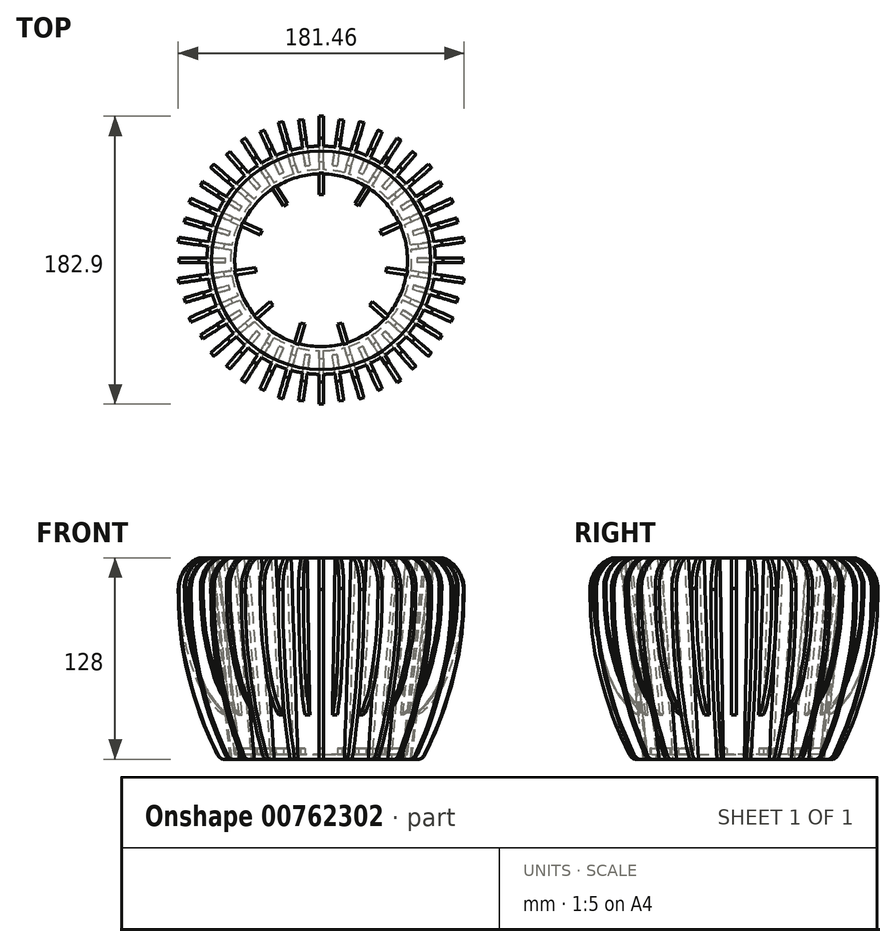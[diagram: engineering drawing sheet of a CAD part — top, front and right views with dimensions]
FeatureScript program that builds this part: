
annotation { "Feature Type Name" : "Feature", "Feature Type Description" : "" }
export const myFeature = defineFeature(function(context is Context, id is Id, definition is map)
    precondition{}
    {
        {
            var Q0;
            Q0=qCreatedBy(makeId("Top.planeOp"),FACE);
            var sketch = newSketch(context, id + "F0", { "sketchPlane" : qUnion([Q0])});
            skCircle(sketch, "E0", {"center": v(0, 0) * mm, "radius": 57.5 * mm});
            skSolve(sketch);
        }
        {
            var Q0;
            Q0=qCreatedBy(makeId("Top.planeOp"),FACE);
            cPlane(context, id + "F1", {"entities" : qUnion([Q0]), "cplaneType" : CPlaneType.OFFSET, "offset" : 128 * mm, "width" : 150 * mm, "height" : 150 * mm});
        }
        {
            var Q0;
            Q0=qCreatedBy(id+"F1.planeOp",FACE);
            var sketch = newSketch(context, id + "F2", { "sketchPlane" : qUnion([Q0])});
            skCircle(sketch, "E1", {"center": v(0, 0) * mm, "radius": 72.5 * mm});
            skSolve(sketch);
        }
        {
            var Q0;
            Q0=makeQuery(id+"F0.imprint","IMPRINT",FACE,{"disambiguationData":[TD([[makeQuery(id+"F0.imprint","IMPRINT",EDGE,{"derivedFrom":sQuery(id+"F0.wireOp",EDGE,"E0")}),1.0]])]});
            var Q1;
            Q1=makeQuery(id+"F2.imprint","IMPRINT",FACE,{"disambiguationData":[TD([[makeQuery(id+"F2.imprint","IMPRINT",EDGE,{"derivedFrom":sQuery(id+"F2.wireOp",EDGE,"E1")}),1.0]])]});
            loft(context, id + "F3", {"sheetProfilesArray" : [{ "sheetProfileEntities" : qUnion([Q0]) }, { "sheetProfileEntities" : qUnion([Q1]) }]});
        }
        {
            var Q0;
            Q0=makeQuery(id+"F3.opLoft","CAP_FACE",FACE,{"disambiguationData":[OSD([makeQuery(id+"F2.imprint","IMPRINT",FACE,{"disambiguationData":[TD([[makeQuery(id+"F2.imprint","IMPRINT",EDGE,{"derivedFrom":sQuery(id+"F2.wireOp",EDGE,"E1")}),1.0]])]})])],"isStart":true});
            var sketch = newSketch(context, id + "F4", { "sketchPlane" : qUnion([Q0])});
            skCircle(sketch, "E2", {"center": v(0, 0) * mm, "radius": 69.5 * mm});
            skSolve(sketch);
        }
        {
            var Q0;
            Q0=makeQuery(id+"F3.opLoft","CAP_FACE",FACE,{"disambiguationData":[OSD([makeQuery(id+"F0.imprint","IMPRINT",FACE,{"disambiguationData":[TD([[makeQuery(id+"F0.imprint","IMPRINT",EDGE,{"derivedFrom":sQuery(id+"F0.wireOp",EDGE,"E0")}),1.0]])]})])],"isStart":true});
            var sketch = newSketch(context, id + "F5", { "sketchPlane" : qUnion([Q0])});
            skCircle(sketch, "E3", {"center": v(0, 0) * mm, "radius": 54.5 * mm});
            skSolve(sketch);
        }
        {
            var Q1;
            Q1=makeQuery(id+"F5.imprint","IMPRINT",FACE,{"disambiguationData":[TD([[makeQuery(id+"F5.imprint","IMPRINT",EDGE,{"derivedFrom":sQuery(id+"F5.wireOp",EDGE,"E3")}),1.0]])]});
            var Q2;
            Q2=makeQuery(id+"F4.imprint","IMPRINT",FACE,{"disambiguationData":[TD([[makeQuery(id+"F4.imprint","IMPRINT",EDGE,{"derivedFrom":sQuery(id+"F4.wireOp",EDGE,"E2")}),1.0]])]});
            loft(context, id + "F6", {"operationType" : NewBodyOperationType.REMOVE, "sheetProfilesArray" : [{ "sheetProfileEntities" : qUnion([Q1]) }, { "sheetProfileEntities" : qUnion([Q2]) }]});
        }
        {
            var Q0;
            Q0=makeQuery(id+"F5.imprint","IMPRINT",FACE,{"disambiguationData":[TD([[makeQuery(id+"F5.imprint","IMPRINT",EDGE,{"derivedFrom":sQuery(id+"F5.wireOp",EDGE,"E3")}),1.0]])]});
            var Q1;
            Q1=makeQuery(id+"F5.imprint","IMPRINT",FACE,{"disambiguationData":[TD([[makeQuery(id+"F5.imprint","IMPRINT",EDGE,{"derivedFrom":sQuery(id+"F5.wireOp",EDGE,"E3")}),-1.0]])]});
            extrude(context, id + "F7", {"entities" : qUnion([Q0, Q1]), "operationType" : NewBodyOperationType.ADD, "oppositeDirection" : true, "depth" : 3 * mm, "offsetDistance" : 25 * mm});
        }
        {
            var Q0;
            Q0=qCreatedBy(makeId("Front.planeOp"),FACE);
            var sketch = newSketch(context, id + "F8", { "sketchPlane" : qUnion([Q0])});
            skLineSegment(sketch, "E4", {"start": v(-1.5, 0) * mm, "end": v(1.5, 0) * mm});
            skLineSegment(sketch, "E5", {"start": v(1.5, 0) * mm, "end": v(1.5, 128) * mm});
            skLineSegment(sketch, "E6", {"start": v(1.5, 128) * mm, "end": v(-1.5, 128) * mm});
            skLineSegment(sketch, "E7", {"start": v(-1.5, 128) * mm, "end": v(-1.5, 0) * mm});
            skSolve(sketch);
        }
        {
            var Q0;
            Q0 = qSketchRegion(id + "F8", true);
            var Q1;
            Q1=makeQuery(id+"F3.opLoft","SWEPT_FACE",FACE,{"disambiguationData":[OSD([sQuery(id+"F0.wireOp",EDGE,"E0"),sQuery(id+"F2.wireOp",EDGE,"E1")])]});
            extrude(context, id + "F9", {"entities" : qUnion([Q0]), "operationType" : NewBodyOperationType.ADD, "oppositeDirection" : true, "depth" : 92.8 * mm, "offsetDistance" : 25 * mm, "hasSecondDirection" : true, "secondDirectionBound" : SecondDirectionBoundingType.UP_TO_SURFACE, "secondDirectionOppositeDirection" : true, "secondDirectionDepth" : 87.6 * mm, "secondDirectionBoundEntityFace" : qUnion([Q1])});
        }
        {
            var Q0;
            Q0=makeQuery(id+"F9.opExtrude","SWEPT_FACE",FACE,{"disambiguationData":[OSD([sQuery(id+"F8.wireOp",EDGE,"E7")])]});
            var sketch = newSketch(context, id + "F10", { "sketchPlane" : qUnion([Q0])});
            skPoint(sketch, "E8", {"position": v(-70.14, 108) * mm});
            skPoint(sketch, "E9", {"position": v(-77.48, 128) * mm});
            skArc(sketch, "E10", {"start": v(-77.48, 128) * mm, "mid": v(-87.61, 120.2) * mm, "end": v(-91.45, 108) * mm});
            skPoint(sketch, "E11", {"position": v(-62.48, 0) * mm});
            skLineSegment(sketch, "E12", {"start": v(-57.48, 0) * mm, "end": v(-62.48, 0) * mm});
            skFitSpline(sketch, "E13", {"points": [v(-62.48, 0) * mm, v(-64.01, 0.32) * mm, v(-65.44, 1.34) * mm, v(-67.06, 4.33) * mm, v(-75.69, 23.58) * mm, v(-88.98, 71.9) * mm, v(-91.45, 108) * mm], "startDerivative": vector(-27.52, 3.42) * mm, "endDerivative": vector(-1.61, 124.86) * mm});
            skLineSegment(sketch, "E14", {"start": v(-72.48, 128) * mm, "end": v(-77.48, 128) * mm});
            skSolve(sketch);
        }
        {
            var Q0;
            {var subQ5=sQuery(id+"F10.wireOp",EDGE,"E10");Q0=makeQuery(id+"F10.imprint","IMPRINT",FACE,{"disambiguationData":[TD([[makeQuery(id+"F10.imprint","IMPRINT",EDGE,{"derivedFrom":subQ5}),-1.0]])]});}
            extrude(context, id + "F11", {"entities" : qUnion([Q0]), "operationType" : NewBodyOperationType.REMOVE, "oppositeDirection" : true, "depth" : 3 * mm, "offsetDistance" : 25 * mm});
        }
        {
            var Q0;
            Q0=qCreatedBy(makeId("Front.planeOp"),FACE);
            var sketch = newSketch(context, id + "F12", { "sketchPlane" : qUnion([Q0])});
            skLineSegment(sketch, "E15", {"start": v(0, 0) * mm, "end": v(0, 133.91) * mm, "construction": true});
            skSolve(sketch);
        }
        {
            var Q0;
            Q0=qCreatedBy(makeId("Right.planeOp"),FACE);
            var sketch = newSketch(context, id + "F13", { "sketchPlane" : qUnion([Q0])});
            skLineSegment(sketch, "E16", {"start": v(1.5, 0) * mm, "end": v(-1.5, 0) * mm, "construction": true});
            skLineSegment(sketch, "E17", {"start": v(-1.5, 0) * mm, "end": v(-1.5, 128) * mm, "construction": true});
            skLineSegment(sketch, "E18", {"start": v(-1.5, 128) * mm, "end": v(1.5, 128) * mm, "construction": true});
            skLineSegment(sketch, "E19", {"start": v(1.5, 128) * mm, "end": v(1.5, 0) * mm, "construction": true});
            skLineSegment(sketch, "E20", {"start": v(1.5, 128) * mm, "end": v(1.5, 28) * mm});
            skLineSegment(sketch, "E21", {"start": v(1.5, 28) * mm, "end": v(-1.5, 28) * mm});
            skLineSegment(sketch, "E22", {"start": v(-1.5, 28) * mm, "end": v(-1.5, 128) * mm});
            skLineSegment(sketch, "E23", {"start": v(-1.5, 128) * mm, "end": v(1.5, 128) * mm});
            skSolve(sketch);
        }
        {
            var Q0;
            Q0 = qSketchRegion(id + "F13", true);
            var Q1;
            Q1=makeQuery(id+"F3.opLoft","SWEPT_FACE",FACE,{"disambiguationData":[OSD([sQuery(id+"F0.wireOp",EDGE,"E0"),sQuery(id+"F2.wireOp",EDGE,"E1")])]});
            extrude(context, id + "F14", {"entities" : qUnion([Q0]), "operationType" : NewBodyOperationType.ADD, "oppositeDirection" : true, "depth" : 98 * mm, "offsetDistance" : 25 * mm, "hasSecondDirection" : true, "secondDirectionBound" : SecondDirectionBoundingType.UP_TO_SURFACE, "secondDirectionOppositeDirection" : true, "secondDirectionDepth" : 82.3 * mm, "secondDirectionBoundEntityFace" : qUnion([Q1])});
        }
        {
            var Q0;
            Q0=makeQuery(id+"F14.opExtrude","SWEPT_FACE",FACE,{"disambiguationData":[OSD([sQuery(id+"F13.wireOp",EDGE,"E22")])]});
            var sketch = newSketch(context, id + "F15", { "sketchPlane" : qUnion([Q0])});
            skLineSegment(sketch, "E24", {"start": v(-72.48, 128) * mm, "end": v(-77.48, 128) * mm});
            skArc(sketch, "E25", {"start": v(-77.48, 128) * mm, "mid": v(-87, 120.23) * mm, "end": v(-90.12, 108.35) * mm});
            skFitSpline(sketch, "E26", {"points": [v(-90.12, 108.35) * mm, v(-87.86, 80.87) * mm, v(-79.15, 50.5) * mm, v(-72.78, 39.24) * mm, v(-64.7, 30.32) * mm, v(-60.76, 28) * mm], "startDerivative": vector(2.75, -100.33) * mm, "endDerivative": vector(34.4, -15.63) * mm});
            skSolve(sketch);
        }
        {
            var Q0;
            {var subQ3=sQuery(id+"F15.wireOp",EDGE,"E25");Q0=makeQuery(id+"F15.imprint","IMPRINT",FACE,{"disambiguationData":[TD([[makeQuery(id+"F15.imprint","IMPRINT",EDGE,{"derivedFrom":subQ3}),-1.0]])]});}
            extrude(context, id + "F16", {"entities" : qUnion([Q0]), "operationType" : NewBodyOperationType.REMOVE, "oppositeDirection" : true, "depth" : 3 * mm, "offsetDistance" : 25 * mm});
        }
        {
            var Q0;
            Q0=makeQuery(id+"F3.opLoft","SWEPT_BODY",BODY,{"disambiguationData":[OSD([makeQuery(id+"F0.imprint","IMPRINT",FACE,{"disambiguationData":[TD([[makeQuery(id+"F0.imprint","IMPRINT",EDGE,{"derivedFrom":sQuery(id+"F0.wireOp",EDGE,"E0")}),1.0]])]}),makeQuery(id+"F2.imprint","IMPRINT",FACE,{"disambiguationData":[TD([[makeQuery(id+"F2.imprint","IMPRINT",EDGE,{"derivedFrom":sQuery(id+"F2.wireOp",EDGE,"E1")}),1.0]])]})])]});
            var Q1;
            Q1=sQuery(id+"F12.wireOp",EDGE,"E15");
            circularPattern(context, id + "F17", {"operationType" : NewBodyOperationType.ADD, "entities" : qUnion([Q0]), "axis" : qUnion([Q1]), "angle" : 360 * degree, "instanceCount" : 22, "equalSpace" : true});
        }
        {
            var Q0;
            Q0=makeQuery(id+"F7.opExtrude","CAP_FACE",FACE,{"disambiguationData":[OSD([sQuery(id+"F0.wireOp",EDGE,"E0")])],"isStart":false});
            var sketch = newSketch(context, id + "F18", { "sketchPlane" : qUnion([Q0])});
            skLineSegment(sketch, "E27", {"start": v(0, 0) * mm, "end": v(0, 54.85) * mm, "construction": true});
            skLineSegment(sketch, "E28", {"start": v(0, 56.85) * mm, "end": v(-1.5, 56.85) * mm});
            skLineSegment(sketch, "E29", {"start": v(-1.5, 56.85) * mm, "end": v(-1.5, 41.85) * mm});
            skLineSegment(sketch, "E30", {"start": v(-1.5, 41.85) * mm, "end": v(1.5, 41.85) * mm});
            skLineSegment(sketch, "E31", {"start": v(1.5, 41.85) * mm, "end": v(1.5, 56.85) * mm});
            skLineSegment(sketch, "E32", {"start": v(1.5, 56.85) * mm, "end": v(0, 56.85) * mm});
            skSolve(sketch);
        }
        {
            var Q0;
            Q0 = qSketchRegion(id + "F18", true);
            extrude(context, id + "F19", {"entities" : qUnion([Q0]), "operationType" : NewBodyOperationType.ADD, "depth" : 4 * mm, "offsetDistance" : 25 * mm});
        }
        {
            var Q0;
            Q0=makeQuery(id+"F3.opLoft","SWEPT_BODY",BODY,{"disambiguationData":[OSD([makeQuery(id+"F0.imprint","IMPRINT",FACE,{"disambiguationData":[TD([[makeQuery(id+"F0.imprint","IMPRINT",EDGE,{"derivedFrom":sQuery(id+"F0.wireOp",EDGE,"E0")}),1.0]])]}),makeQuery(id+"F2.imprint","IMPRINT",FACE,{"disambiguationData":[TD([[makeQuery(id+"F2.imprint","IMPRINT",EDGE,{"derivedFrom":sQuery(id+"F2.wireOp",EDGE,"E1")}),1.0]])]})])]});
            var Q1;
            Q1=sQuery(id+"F12.wireOp",EDGE,"E15");
            circularPattern(context, id + "F20", {"operationType" : NewBodyOperationType.ADD, "entities" : qUnion([Q0]), "axis" : qUnion([Q1]), "angle" : 360 * degree, "instanceCount" : 11, "equalSpace" : true});
        }
    });
